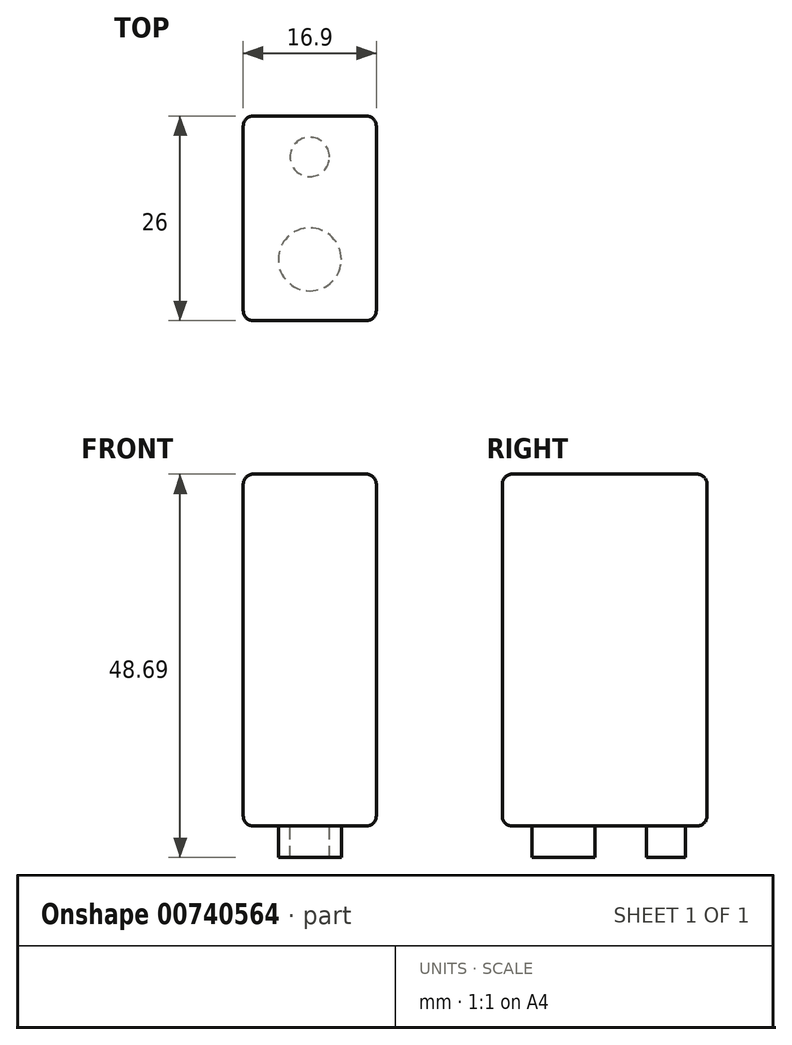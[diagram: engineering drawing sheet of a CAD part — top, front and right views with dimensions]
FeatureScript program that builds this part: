
annotation { "Feature Type Name" : "Feature", "Feature Type Description" : "" }
export const myFeature = defineFeature(function(context is Context, id is Id, definition is map)
    precondition{}
    {
        {
            var Q0;
            Q0=qCreatedBy(makeId("Top.planeOp"),FACE);
            var sketch = newSketch(context, id + "F0", { "sketchPlane" : qUnion([Q0])});
            skLineSegment(sketch, "E0.bottom", {"start": v(8.45, 13) * mm, "end": v(-8.45, 13) * mm});
            skLineSegment(sketch, "E0.top", {"start": v(8.45, -13) * mm, "end": v(-8.45, -13) * mm});
            skLineSegment(sketch, "E0.left", {"start": v(8.45, 13) * mm, "end": v(8.45, -13) * mm});
            skLineSegment(sketch, "E0.right", {"start": v(-8.45, 13) * mm, "end": v(-8.45, -13) * mm});
            skPoint(sketch, "E0.middle", {"position": v(0, 0) * mm});
            skSolve(sketch);
        }
        {
            var Q0;
            Q0=makeQuery(id+"F0.imprint","IMPRINT",FACE,{"disambiguationData":[TD([[makeQuery(id+"F0.imprint","IMPRINT",EDGE,{"derivedFrom":sQuery(id+"F0.wireOp",EDGE,"E0.bottom")}),1.0]])]});
            extrude(context, id + "F1", {"entities" : qUnion([Q0]), "depth" : 44.7 * mm, "offsetDistance" : 25.4 * mm});
        }
        {
            var Q0;
            Q0=qCreatedBy(makeId("Top.planeOp"),FACE);
            var sketch = newSketch(context, id + "F2", { "sketchPlane" : qUnion([Q0])});
            skCircle(sketch, "E1", {"center": v(0, -5.2) * mm, "radius": 4 * mm});
            skCircle(sketch, "E2", {"center": v(0, 7.8) * mm, "radius": 2.5 * mm});
            skSolve(sketch);
        }
        {
            var Q0;
            Q0=makeQuery(id+"F2.imprint","IMPRINT",FACE,{"disambiguationData":[TD([[makeQuery(id+"F2.imprint","IMPRINT",EDGE,{"derivedFrom":sQuery(id+"F2.wireOp",EDGE,"E2")}),1.0]])]});
            var Q1;
            Q1=makeQuery(id+"F2.imprint","IMPRINT",FACE,{"disambiguationData":[TD([[makeQuery(id+"F2.imprint","IMPRINT",EDGE,{"derivedFrom":sQuery(id+"F2.wireOp",EDGE,"E1")}),1.0]])]});
            extrude(context, id + "F3", {"entities" : qUnion([Q0, Q1]), "operationType" : NewBodyOperationType.ADD, "oppositeDirection" : true, "depth" : 4 * mm, "offsetDistance" : 25.4 * mm});
        }
        {
            var Q0;
            Q0=makeQuery(id+"F1.opExtrude","CAP_EDGE",EDGE,{"disambiguationData":[OSD([sQuery(id+"F0.wireOp",EDGE,"E0.top")])],"isStart":true});
            var Q1;
            Q1=makeQuery(id+"F1.opExtrude","CAP_EDGE",EDGE,{"disambiguationData":[OSD([sQuery(id+"F0.wireOp",EDGE,"E0.right")])],"isStart":true});
            var Q2;
            Q2=makeQuery(id+"F1.opExtrude","CAP_EDGE",EDGE,{"disambiguationData":[OSD([sQuery(id+"F0.wireOp",EDGE,"E0.bottom")])],"isStart":true});
            var Q3;
            Q3=makeQuery(id+"F1.opExtrude","CAP_EDGE",EDGE,{"disambiguationData":[OSD([sQuery(id+"F0.wireOp",EDGE,"E0.left")])],"isStart":true});
            var Q4;
            Q4=makeQuery(id+"F1.opExtrude","SWEPT_EDGE",EDGE,{"disambiguationData":[OSD([sQuery(id+"F0.wireOp",EDGE,"E0.top"),sQuery(id+"F0.wireOp",EDGE,"E0.right")])]});
            var Q5;
            Q5=makeQuery(id+"F1.opExtrude","SWEPT_EDGE",EDGE,{"disambiguationData":[OSD([sQuery(id+"F0.wireOp",EDGE,"E0.bottom"),sQuery(id+"F0.wireOp",EDGE,"E0.right")])]});
            var Q6;
            Q6=makeQuery(id+"F1.opExtrude","SWEPT_EDGE",EDGE,{"disambiguationData":[OSD([sQuery(id+"F0.wireOp",EDGE,"E0.top"),sQuery(id+"F0.wireOp",EDGE,"E0.left")])]});
            var Q7;
            Q7=makeQuery(id+"F1.opExtrude","CAP_EDGE",EDGE,{"disambiguationData":[OSD([sQuery(id+"F0.wireOp",EDGE,"E0.top")])],"isStart":false});
            var Q8;
            Q8=makeQuery(id+"F1.opExtrude","CAP_EDGE",EDGE,{"disambiguationData":[OSD([sQuery(id+"F0.wireOp",EDGE,"E0.right")])],"isStart":false});
            var Q9;
            Q9=makeQuery(id+"F1.opExtrude","SWEPT_EDGE",EDGE,{"disambiguationData":[OSD([sQuery(id+"F0.wireOp",EDGE,"E0.bottom"),sQuery(id+"F0.wireOp",EDGE,"E0.left")])]});
            var Q10;
            Q10=makeQuery(id+"F1.opExtrude","CAP_EDGE",EDGE,{"disambiguationData":[OSD([sQuery(id+"F0.wireOp",EDGE,"E0.left")])],"isStart":false});
            var Q11;
            Q11=makeQuery(id+"F1.opExtrude","CAP_EDGE",EDGE,{"disambiguationData":[OSD([sQuery(id+"F0.wireOp",EDGE,"E0.bottom")])],"isStart":false});
            fillet(context, id + "F4", {"entities" : qUnion([Q0, Q1, Q2, Q3, Q4, Q5, Q6, Q7, Q8, Q9, Q10, Q11]), "radius" : 1.27 * mm, "tangentPropagation" : true, "allowEdgeOverflow" : false});
        }
    });
